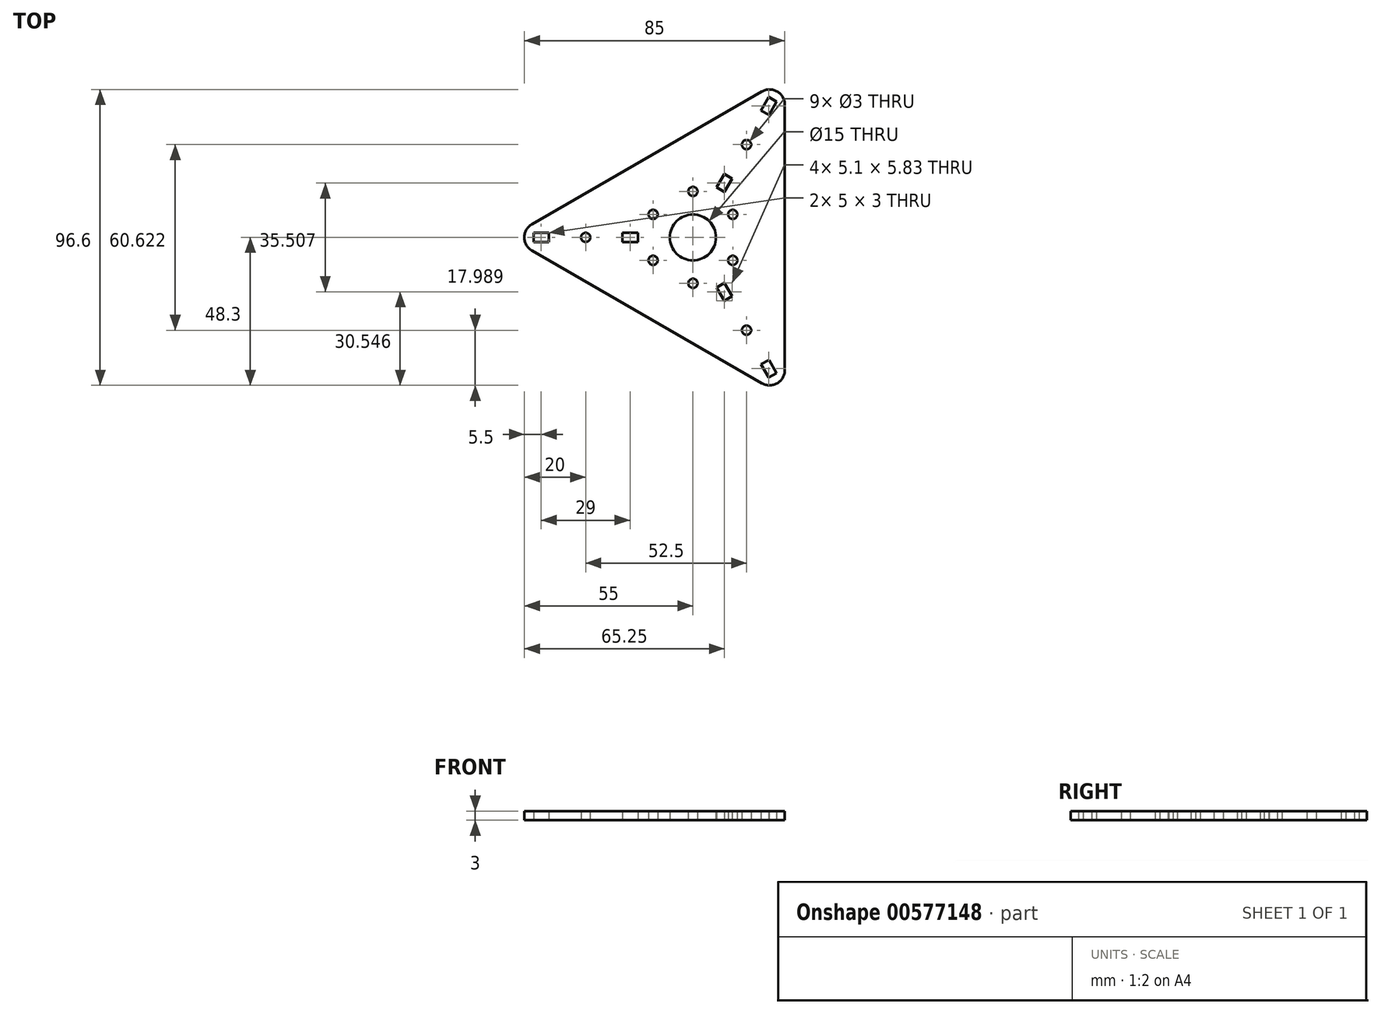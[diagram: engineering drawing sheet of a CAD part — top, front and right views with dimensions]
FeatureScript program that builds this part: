
annotation { "Feature Type Name" : "Feature", "Feature Type Description" : "" }
export const myFeature = defineFeature(function(context is Context, id is Id, definition is map)
    precondition{}
    {
        {
            var Q0;
            Q0=qCreatedBy(makeId("Top.planeOp"),FACE);
            var sketch = newSketch(context, id + "F0", { "sketchPlane" : qUnion([Q0])});
            skCircle(sketch, "E0.cCircle", {"center": v(0, 0) * mm, "radius": 60 * mm, "construction": true});
            skLineSegment(sketch, "E0.0", {"start": v(-52.5, 4.33) * mm, "end": v(22.5, 47.63) * mm});
            skLineSegment(sketch, "E0.1", {"start": v(30, 43.3) * mm, "end": v(30, -43.3) * mm});
            skLineSegment(sketch, "E0.2", {"start": v(22.5, -47.63) * mm, "end": v(-52.5, -4.33) * mm});
            skPoint(sketch, "E1.visualSharp", {"position": v(-60, 0) * mm});
            skArc(sketch, "E1.filletArc", {"start": v(-52.5, 4.33) * mm, "mid": v(-55, 0) * mm, "end": v(-52.5, -4.33) * mm});
            skPoint(sketch, "E2.visualSharp", {"position": v(30, 51.96) * mm});
            skArc(sketch, "E2.filletArc", {"start": v(30, 43.3) * mm, "mid": v(27.5, 47.63) * mm, "end": v(22.5, 47.63) * mm});
            skPoint(sketch, "E3.visualSharp", {"position": v(30, -51.96) * mm});
            skArc(sketch, "E3.filletArc", {"start": v(22.5, -47.63) * mm, "mid": v(27.5, -47.63) * mm, "end": v(30, -43.3) * mm});
            skLineSegment(sketch, "E4.bottom", {"start": v(-47, -1.5) * mm, "end": v(-52, -1.5) * mm});
            skLineSegment(sketch, "E4.top", {"start": v(-47, 1.5) * mm, "end": v(-52, 1.5) * mm});
            skLineSegment(sketch, "E4.left", {"start": v(-47, -1.5) * mm, "end": v(-47, 1.5) * mm});
            skLineSegment(sketch, "E4.right", {"start": v(-52, -1.5) * mm, "end": v(-52, 1.5) * mm});
            skPoint(sketch, "E4.middle", {"position": v(-49.5, 0) * mm});
            skLineSegment(sketch, "E5.bottom", {"start": v(-18, -1.5) * mm, "end": v(-23, -1.5) * mm});
            skLineSegment(sketch, "E5.top", {"start": v(-18, 1.5) * mm, "end": v(-23, 1.5) * mm});
            skLineSegment(sketch, "E5.left", {"start": v(-18, -1.5) * mm, "end": v(-18, 1.5) * mm});
            skLineSegment(sketch, "E5.right", {"start": v(-23, -1.5) * mm, "end": v(-23, 1.5) * mm});
            skPoint(sketch, "E5.middle", {"position": v(-20.5, 0) * mm});
            skPoint(sketch, "E6", {"position": v(-35, 0) * mm});
            skCircle(sketch, "E7", {"center": v(-35, 0) * mm, "radius": 1.5 * mm});
            skLineSegment(sketch, "E8.1.0", {"start": v(24.8, -39.95) * mm, "end": v(22.2, -41.45) * mm});
            skLineSegment(sketch, "E8.1.1", {"start": v(24.8, -39.95) * mm, "end": v(27.3, -44.28) * mm});
            skLineSegment(sketch, "E8.1.2", {"start": v(27.3, -44.28) * mm, "end": v(24.7, -45.78) * mm});
            skLineSegment(sketch, "E8.1.3", {"start": v(22.2, -41.45) * mm, "end": v(24.7, -45.78) * mm});
            skCircle(sketch, "E8.1.4", {"center": v(17.5, -30.31) * mm, "radius": 1.5 * mm});
            skLineSegment(sketch, "E8.1.5", {"start": v(7.7, -16.34) * mm, "end": v(10.2, -20.67) * mm});
            skLineSegment(sketch, "E8.1.6", {"start": v(12.8, -19.17) * mm, "end": v(10.2, -20.67) * mm});
            skLineSegment(sketch, "E8.1.7", {"start": v(10.3, -14.84) * mm, "end": v(7.7, -16.34) * mm});
            skLineSegment(sketch, "E8.1.8", {"start": v(10.3, -14.84) * mm, "end": v(12.8, -19.17) * mm});
            skLineSegment(sketch, "E8.2.0", {"start": v(22.2, 41.45) * mm, "end": v(24.8, 39.95) * mm});
            skLineSegment(sketch, "E8.2.1", {"start": v(22.2, 41.45) * mm, "end": v(24.7, 45.78) * mm});
            skLineSegment(sketch, "E8.2.2", {"start": v(24.7, 45.78) * mm, "end": v(27.3, 44.28) * mm});
            skLineSegment(sketch, "E8.2.3", {"start": v(24.8, 39.95) * mm, "end": v(27.3, 44.28) * mm});
            skCircle(sketch, "E8.2.4", {"center": v(17.5, 30.31) * mm, "radius": 1.5 * mm});
            skLineSegment(sketch, "E8.2.5", {"start": v(10.3, 14.84) * mm, "end": v(12.8, 19.17) * mm});
            skLineSegment(sketch, "E8.2.6", {"start": v(10.2, 20.67) * mm, "end": v(12.8, 19.17) * mm});
            skLineSegment(sketch, "E8.2.7", {"start": v(7.7, 16.34) * mm, "end": v(10.3, 14.84) * mm});
            skLineSegment(sketch, "E8.2.8", {"start": v(7.7, 16.34) * mm, "end": v(10.2, 20.67) * mm});
            skCircle(sketch, "E9", {"center": v(0, 0) * mm, "radius": 7.5 * mm});
            skCircle(sketch, "E10", {"center": v(-13, 7.5) * mm, "radius": 1.5 * mm});
            skLineSegment(sketch, "E11", {"start": v(0, 0) * mm, "end": v(-38.74, 22.37) * mm, "construction": true});
            skCircle(sketch, "E12.1.0", {"center": v(-13, -7.5) * mm, "radius": 1.5 * mm});
            skCircle(sketch, "E12.2.0", {"center": v(0, -15) * mm, "radius": 1.5 * mm});
            skCircle(sketch, "E12.3.0", {"center": v(13, -7.5) * mm, "radius": 1.5 * mm});
            skCircle(sketch, "E12.4.0", {"center": v(13, 7.5) * mm, "radius": 1.5 * mm});
            skCircle(sketch, "E12.5.0", {"center": v(0, 15) * mm, "radius": 1.5 * mm});
            skSolve(sketch);
        }
        {
            var Q0;
            Q0=qSketchRegion(id+"F0",true);
            extrude(context, id + "F1", {"entities" : qUnion([Q0]), "endBound" : BoundingType.SYMMETRIC, "depth" : 3 * mm});
        }
    });
